# Revit family: Drain_Floor_Conical_8-Inch_Diameter-Zurn-Z1802-8B
name_source: partatom
category: Plumbing Fixtures
units: mm (PartAtom-declared; Revit-internal decimal feet)

## family parameters
Always vertical = Yes
Cut with Voids When Loaded = No
Maintain Annotation Orientation = No
OmniClass Number = 23.70.50.21.24
OmniClass Title = Waste Water Drains
Part Type = Normal
Room Calculation Point = No
Round Connector Dimension = Use Diameter
Shared = No
Work Plane-Based = No

## types (48) — shared parameters
Assembly Code = D2030300
CW Connection = No
HW Connection = No
Manufacturer = Zurn Water, LLC
Manufacurer Brand = Zurn
Model = Z1802-8B
Top Diameter = 8.25 "
URL = www.zurn.com
Vent Connection = No
Waste Connection = Yes
zero-valued in all types: Default Elevation

## per-type parameters (varying)
| type | Coupling | Description | H3_Permeter_Grate | Main Material | Perforated Grate | Pipe Size_A (Nominal) Diameter | Pipe Size_A Outer Diameter | Product Documentation Link | Product Page URL | Product data url | Sump Depth | Top Depth for Grate | Type Comments |
| Z1802-8B-2NH Outlet | No | 8 Inch Diameter Conical Sanitary Floor Drain | No | Steel - Zurn - Stainless Type 304 (CF8) | Yes | 2 " | 2.375 " | https://files.zurn.com | https://www.zurn.com |  | 3.5 " | 0.563 " | Z1802-8B-2NH (Sch 10 Outlet 3" Length) |
| Z1802-8B-3NH Outlet | No | 8 Inch Diameter Conical Sanitary Floor Drain | No | Steel - Zurn - Stainless Type 304 (CF8) | Yes | 3 " | 3.5 " | https://files.zurn.com | https://www.zurn.com |  | 3.5 " | 0.563 " | Z1802-3NH (Sch 10 Outlet 3" Length) |
| Z1802-8B-4NH Outlet | No | 8 Inch Diameter Conical Sanitary Floor Drain | No | Steel - Zurn - Stainless Type 304 (CF8) | Yes | 4 " | 4.5 " |  |  |  | 3.5 " | 0.563 " | Z1802-4NH (Sch 10 Outlet 3" Length) |
| ZM1802-8B-2NH Outlet | No | 8 Inch Diameter Conical Sanitary Floor Drain | No | Steel - Zurn - Stainless Type 316 (CF8M) | Yes | 2 " | 2.375 " |  |  |  | 3.5 " | 0.563 " | ZM1802-2NH (Sch 10 Outlet 3" Length) |
| ZM1802-8B-3NH Outlet | No | 8 Inch Diameter Conical Sanitary Floor Drain | No | Steel - Zurn - Stainless Type 316 (CF8M) | Yes | 3 " | 3.5 " |  |  |  | 3.5 " | 0.563 " | ZM1802-8B-3NH (Sch 10 Outlet 3" Length) |
| ZM1802-8B-4NH Outlet | No | 8 Inch Diameter Conical Sanitary Floor Drain | No | Steel - Zurn - Stainless Type 316 (CF8M) | Yes | 4 " | 4.5 " |  |  |  | 3.5 " | 0.563 " | ZM1802-8B-4NH (Sch 10 Outlet 3" Length) |
| Z1802-8B-2A Outlet | Yes | 8 Inch Diameter Conical Sanitary Floor Drain | No | Steel - Zurn - Stainless Type 304 (CF8) | Yes | 2 " | 2.375 " | https://files.zurn.com | https://www.zurn.com | https://bimobject.com | 3.5 " | 0.563 " | Z1802-8B-2A (Adjustable Threaded Outlet Lenght 4-3/4 Min - 6.0 Max) |
| Z1802-8B-3A Outlet | Yes | 8 Inch Diameter Conical Sanitary Floor Drain | No | Steel - Zurn - Stainless Type 304 (CF8) | Yes | 3 " | 3.5 " | https://files.zurn.com | https://www.zurn.com |  | 3.5 " | 0.563 " | Z1802-8B-3A (Adjustable Threaded Outlet Lenght 3-1/2 Min - 5-3/4 Max) |
| Z1802-8B-4A Outlet | Yes | 8 Inch Diameter Conical Sanitary Floor Drain | No | Steel - Zurn - Stainless Type 304 (CF8) | Yes | 4 " | 4.5 " |  | https://www.zurn.com |  | 3.5 " | 0.563 " | Z1802-8B-4A (Adjustable Threaded Outlet Length 3-1/2 Min - 5-3/4 Max) |
| ZM1802-8B-2A Outlet | Yes | 8 Inch Diameter Conical Sanitary Floor Drain | No | Steel - Zurn - Stainless Type 316 (CF8M) | Yes | 2 " | 2.375 " |  |  |  | 3.5 " | 0.563 " | ZM1802-8B-2A (Adjustable Threaded Outlet Lenght 4-3/4 Min - 6.0 Max) |
| ZM1802-8B-3A Outlet | Yes | 8 Inch Diameter Conical Sanitary Floor Drain | No | Steel - Zurn - Stainless Type 316 (CF8M) | Yes | 3 " | 3.5 " |  |  |  | 3.5 " | 0.563 " | Z1802-8B-3A (Adjustable Threaded Outlet Lenght 3-1/2 Min - 5-3/4 Max) |
| ZM1802-8B-4A Outlet | Yes | 8 Inch Diameter Conical Sanitary Floor Drain | No | Steel - Zurn - Stainless Type 316 (CF8M) | Yes | 4 " | 4.5 " |  |  |  | 3.5 " | 0.563 " | Z1802-8B-4A (Adjustable Threaded Outlet Lenght 3-1/2 Min - 5-3/4 Max) |
| Z1802-8B-H3-2NH Outlet | No | 8 Inch Diameter Conical Sanitary Floor Drain w/ Extra-Heavy-Duty Perimeter Gap Grate | Yes | Steel - Zurn - Stainless Type 304 (CF8) | No | 2 " | 2.375 " |  |  |  | 3.75 " | 0.813 " | Z1802-8B-H3-2NH (Sch 10 Outlet 3" Length) |
| Z1802-8B-H3-2A Outlet | Yes | 8 Inch Diameter Conical Sanitary Floor Drain w/ Extra-Heavy-Duty Perimeter Gap Grate | Yes | Steel - Zurn - Stainless Type 304 (CF8) | No | 2 " | 2.375 " |  |  |  | 3.75 " | 0.813 " | Z1802-8B-H3-2A (Adjustable Threaded Outlet Length 4-3/4 Min - 6.0 Max) |
| Z1802-8B-H3-3A Outlet | Yes | 8 Inch Diameter Conical Sanitary Floor Drain w/ Extra-Heavy-Duty Perimeter Gap Grate | Yes | Steel - Zurn - Stainless Type 304 (CF8) | No | 3 " | 3.5 " |  |  |  | 3.75 " | 0.813 " | Z1802-8B-H3-3A (Adjustable Threaded Outlet Lenght 3-1/2 Min - 5-3/4 Max) |
| Z1802-8B-H3-3NH Outlet | No | 8 Inch Diameter Conical Sanitary Floor Drain w/ Extra-Heavy-Duty Perimeter Gap Grate | Yes | Steel - Zurn - Stainless Type 304 (CF8) | No | 3 " | 3.5 " |  |  |  | 3.75 " | 0.813 " | Z1802-8B-H3-3NH (Sch 10 Outlet 3" Length) |
| Z1802-8B-H3-4A Outlet | Yes | 8 Inch Diameter Conical Sanitary Floor Drain w/ Extra-Heavy-Duty Perimeter Gap Grate | Yes | Steel - Zurn - Stainless Type 304 (CF8) | No | 4 " | 4.5 " |  |  |  | 3.75 " | 0.813 " | Z1802-8B-H3-4A (Adjustable Threaded Outlet Lenght 3-1/2 Min - 5-3/4 Max) |
| Z1802-8B-H3-4NH Outlet | No | 8 Inch Diameter Conical Sanitary Floor Drain w/ Extra-Heavy-Duty Perimeter Gap Grate | Yes | Steel - Zurn - Stainless Type 304 (CF8) | No | 4 " | 4.5 " |  |  |  | 3.75 " | 0.813 " | Z1802-8B-H3-4NH (Sch 10 Outlet 3" Length) |
| ZM1802-8B-H3-2A Outlet | Yes | 8 Inch Diameter Conical Sanitary Floor Drain w/ Extra-Heavy-Duty Perimeter Gap Grate | Yes | Steel - Zurn - Stainless Type 316 (CF8M) | No | 2 " | 2.375 " | https://files.zurn.com | https://www.zurn.com |  | 3.75 " | 0.813 " | ZM1802-H3-8B-2A (Adjustable Threaded Outlet Lenght 4-3/4 Min - 6.0 Max) |
| ZM1802-8B-H3-2NH Outlet | No | 8 Inch Diameter Conical Sanitary Floor Drain w/ Extra-Heavy-Duty Perimeter Gap Grate | Yes | Steel - Zurn - Stainless Type 316 (CF8M) | No | 2 " | 2.375 " |  |  |  | 3.75 " | 0.813 " | ZM1802-8B-H3-2NH (Sch 10 Outlet 3" Length) |
| ZM1802-8B-H3-3A Outlet | Yes | 8 Inch Diameter Conical Sanitary Floor Drain w/ Extra-Heavy-Duty Perimeter Gap Grate | Yes | Steel - Zurn - Stainless Type 316 (CF8M) | No | 3 " | 3.5 " |  |  |  | 3.75 " | 0.813 " | ZM1802-8B-H3-3A (Adjustable Threaded Outlet Lenght 3-1/2 Min - 5-3/4 Max) |
| ZM1802-8B-H3-4A Outlet | Yes | 8 Inch Diameter Conical Sanitary Floor Drain w/ Extra-Heavy-Duty Perimeter Gap Grate | Yes | Steel - Zurn - Stainless Type 316 (CF8M) | No | 4 " | 4.5 " |  |  |  | 3.75 " | 0.813 " | ZM1802-8B-H3-4A (Adjustable Threaded Outlet Lenght 3-1/2 Min - 5-3/4 Max) |
| ZM1802-8B-H3-3NH Outlet | No | 8 Inch Diameter Conical Sanitary Floor Drain w/ Extra-Heavy-Duty Perimeter Gap Grate | Yes | Steel - Zurn - Stainless Type 316 (CF8M) | No | 3 " | 3.5 " |  |  |  | 3.75 " | 0.813 " | ZM1802-8B-H3-3NH (Sch 10 Outlet 3" Length) |
| ZM1802-8B-H3-4NH Outlet | No | 8 Inch Diameter Conical Sanitary Floor Drain w/ Extra-Heavy-Duty Perimeter Gap Grate | Yes | Steel - Zurn - Stainless Type 316 (CF8M) | No | 4 " | 4.5 " |  |  |  | 3.75 " | 0.813 " | ZM1802-8B-H3-4NH (Sch 10 Outlet 3" Length) |
| Z1802-8B-2BW Outlet | No | 8 Inch Diameter Conical Sanitary Floor Drain | No | Steel - Zurn - Stainless Type 304 (CF8) | Yes | 2 " | 2.375 " | https://files.zurn.com | https://www.zurn.com |  | 3.5 " | 0.563 " | Z1802-8B-2BW (Sch 40 Outlet 3" Length) |
| Z1802-8B-2IP Outlet | No | 8 Inch Diameter Conical Sanitary Floor Drain | No | Steel - Zurn - Stainless Type 304 (CF8) | Yes | 2 " | 2.375 " | https://files.zurn.com | https://www.zurn.com |  | 3.5 " | 0.563 " | Z1802-8B-2IP (Outlet 3" Length) |
| Z1802-8B-3BW Outlet | No | 8 Inch Diameter Conical Sanitary Floor Drain | No | Steel - Zurn - Stainless Type 304 (CF8) | Yes | 3 " | 3.5 " | https://files.zurn.com | https://www.zurn.com |  | 3.5 " | 0.563 " | Z1802-3BW (Sch 40 Outlet 3" Length) |
| Z1802-8B-3IP Outlet | No | 8 Inch Diameter Conical Sanitary Floor Drain | No | Steel - Zurn - Stainless Type 304 (CF8) | Yes | 3 " | 3.5 " | https://files.zurn.com | https://www.zurn.com |  | 3.5 " | 0.563 " | Z1802-3IP (Outlet 3" Length) |
| Z1802-8B-4BW Outlet | No | 8 Inch Diameter Conical Sanitary Floor Drain | No | Steel - Zurn - Stainless Type 304 (CF8) | Yes | 4 " | 4.5 " |  |  |  | 3.5 " | 0.563 " | Z1802-4BW (Sch 40 Outlet 3" Length) |
| Z1802-8B-4IP Outlet | No | 8 Inch Diameter Conical Sanitary Floor Drain | No | Steel - Zurn - Stainless Type 304 (CF8) | Yes | 4 " | 4.5 " |  |  |  | 3.5 " | 0.563 " | Z1802-4IP (Outlet 3" Length) |
| Z1802-8B-H3-3BW Outlet | No | 8 Inch Diameter Conical Sanitary Floor Drain w/ Extra-Heavy-Duty Perimeter Gap Grate | Yes | Steel - Zurn - Stainless Type 304 (CF8) | No | 3 " | 3.5 " |  |  |  | 3.75 " | 0.813 " | Z1802-8B-H3-3BW (Sch 40 Outlet 3" Length) |
| Z1802-8B-H3-3IP Outlet | No | 8 Inch Diameter Conical Sanitary Floor Drain w/ Extra-Heavy-Duty Perimeter Gap Grate | Yes | Steel - Zurn - Stainless Type 304 (CF8) | No | 3 " | 3.5 " |  |  |  | 3.75 " | 0.813 " | Z1802-8B-H3-3IP (Outlet 3" Length) |
| Z1802-8B-H3-4BW Outlet | No | 8 Inch Diameter Conical Sanitary Floor Drain w/ Extra-Heavy-Duty Perimeter Gap Grate | Yes | Steel - Zurn - Stainless Type 304 (CF8) | No | 4 " | 4.5 " |  |  |  | 3.75 " | 0.813 " | Z1802-8B-H3-4BW (Sch 40 Outlet 3" Length) |
| Z1802-8B-H3-4IP Outlet | No | 8 Inch Diameter Conical Sanitary Floor Drain w/ Extra-Heavy-Duty Perimeter Gap Grate | Yes | Steel - Zurn - Stainless Type 304 (CF8) | No | 4 " | 4.5 " |  |  |  | 3.75 " | 0.813 " | Z1802-8B-H3-4IP (Outlet 3" Length) |
| ZM1802-8B-2BW Outlet | No | 8 Inch Diameter Conical Sanitary Floor Drain | No | Steel - Zurn - Stainless Type 316 (CF8M) | Yes | 2 " | 2.375 " |  |  |  | 3.5 " | 0.563 " | ZM1802-2BW (Sch 40 Outlet 3" Length) |
| ZM1802-8B-2IP Outlet | No | 8 Inch Diameter Conical Sanitary Floor Drain | No | Steel - Zurn - Stainless Type 316 (CF8M) | Yes | 2 " | 2.375 " |  |  |  | 3.5 " | 0.563 " | ZM1802-2IP (Outlet 3" Length) |
| ZM1802-8B-3BW Outlet | No | 8 Inch Diameter Conical Sanitary Floor Drain | No | Steel - Zurn - Stainless Type 316 (CF8M) | Yes | 3 " | 3.5 " |  |  |  | 3.5 " | 0.563 " | ZM1802-8B-3BW (Sch 40 Outlet 3" Length) |
| ZM1802-8B-3IP Outlet | No | 8 Inch Diameter Conical Sanitary Floor Drain | No | Steel - Zurn - Stainless Type 316 (CF8M) | Yes | 3 " | 3.5 " |  |  |  | 3.5 " | 0.563 " | ZM1802-8B-3IP (Outlet 3" Length) |
| ZM1802-8B-4BW Outlet | No | 8 Inch Diameter Conical Sanitary Floor Drain | No | Steel - Zurn - Stainless Type 316 (CF8M) | Yes | 4 " | 4.5 " |  |  |  | 3.5 " | 0.563 " | ZM1802-8B-4BW (Sch 40 Outlet 3" Length) |
| ZM1802-8B-4IP Outlet | No | 8 Inch Diameter Conical Sanitary Floor Drain | No | Steel - Zurn - Stainless Type 316 (CF8M) | Yes | 4 " | 4.5 " |  |  |  | 3.5 " | 0.563 " | ZM1802-8B-4IP (Outlet 3" Length) |
| ZM1802-8B-H3-2BW Outlet | No | 8 Inch Diameter Conical Sanitary Floor Drain w/ Extra-Heavy-Duty Perimeter Gap Grate | Yes | Steel - Zurn - Stainless Type 316 (CF8M) | No | 2 " | 2.375 " |  |  |  | 3.75 " | 0.813 " | ZM1802-8B-H3-2BW (Sch 40 Outlet 3" Length) |
| ZM1802-8B-H3-2IP Outlet | No | 8 Inch Diameter Conical Sanitary Floor Drain w/ Extra-Heavy-Duty Perimeter Gap Grate | Yes | Steel - Zurn - Stainless Type 316 (CF8M) | No | 2 " | 2.375 " |  |  |  | 3.75 " | 0.813 " | ZM1802-8B-H3-2IP (Outlet 3" Length) |
| ZM1802-8B-H3-3BW Outlet | No | 8 Inch Diameter Conical Sanitary Floor Drain w/ Extra-Heavy-Duty Perimeter Gap Grate | Yes | Steel - Zurn - Stainless Type 316 (CF8M) | No | 3 " | 3.5 " |  |  |  | 3.75 " | 0.813 " | ZM1802-8B-H3-3BW (Sch 40 Outlet 3" Length) |
| ZM1802-8B-H3-3IP Outlet | No | 8 Inch Diameter Conical Sanitary Floor Drain w/ Extra-Heavy-Duty Perimeter Gap Grate | Yes | Steel - Zurn - Stainless Type 316 (CF8M) | No | 3 " | 3.5 " |  |  |  | 3.75 " | 0.813 " | ZM1802-8B-H3-3IP (Outlet 3" Length) |
| ZM1802-8B-H3-4BW Outlet | No | 8 Inch Diameter Conical Sanitary Floor Drain w/ Extra-Heavy-Duty Perimeter Gap Grate | Yes | Steel - Zurn - Stainless Type 316 (CF8M) | No | 4 " | 4.5 " |  |  |  | 3.75 " | 0.813 " | ZM1802-8B-H3-4BW (Sch 40 Outlet 3" Length) |
| ZM1802-8B-H3-4IP Outlet | No | 8 Inch Diameter Conical Sanitary Floor Drain w/ Extra-Heavy-Duty Perimeter Gap Grate | Yes | Steel - Zurn - Stainless Type 316 (CF8M) | No | 4 " | 4.5 " |  |  |  | 3.75 " | 0.813 " | ZM1802-8B-H3-4IP (Outlet 3" Length) |
| Z1802-8B-H3-2BW Outlet | No | 8 Inch Diameter Conical Sanitary Floor Drain w/ Extra-Heavy-Duty Perimeter Gap Grate | Yes | Steel - Zurn - Stainless Type 304 (CF8) | No | 2 " | 2.375 " |  |  |  | 3.75 " | 0.813 " | Z1802-8B-H3-2BW (Sch 40 Outlet 3" Length) |
| Z1802-8B-H3-2IP Outlet | No | 8 Inch Diameter Conical Sanitary Floor Drain w/ Extra-Heavy-Duty Perimeter Gap Grate | Yes | Steel - Zurn - Stainless Type 304 (CF8) | No | 2 " | 2.375 " |  |  |  | 3.75 " | 0.813 " | Z1802-8B-H3-2IP (Outlet 3" Length) |

## geometry (parser evidence)
native form markers: Sweep x2
no freeform markers — native parametric forms only
